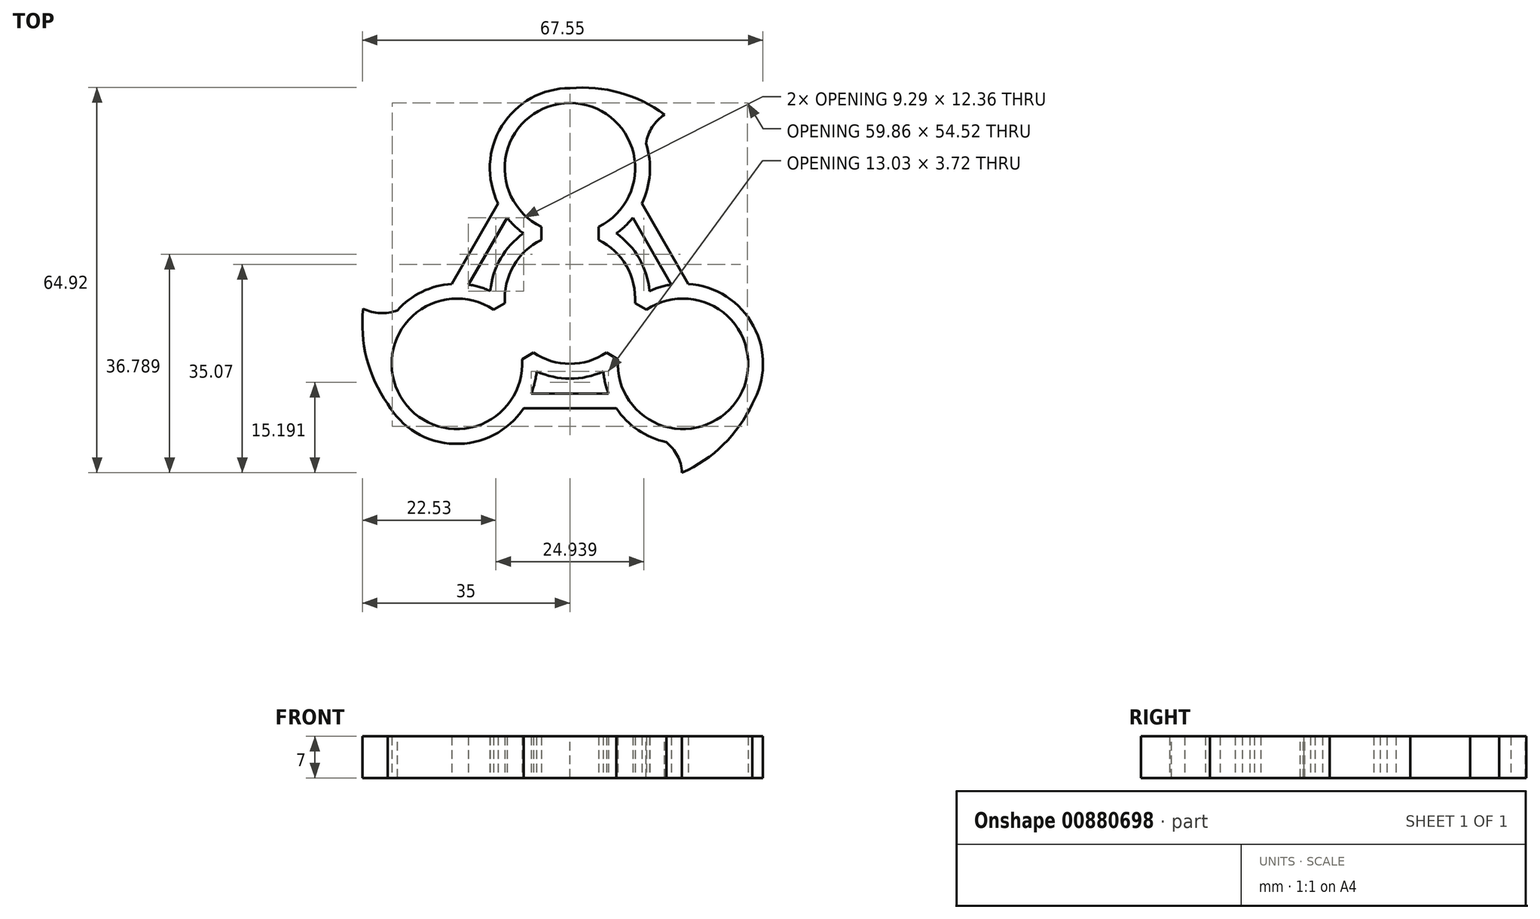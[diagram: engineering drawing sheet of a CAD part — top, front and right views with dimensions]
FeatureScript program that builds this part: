
annotation { "Feature Type Name" : "Feature", "Feature Type Description" : "" }
export const myFeature = defineFeature(function(context is Context, id is Id, definition is map)
    precondition{}
    {
        {
            var Q0;
            Q0=qCreatedBy(makeId("Top.planeOp"),FACE);
            var sketch = newSketch(context, id + "F0", { "sketchPlane" : qUnion([Q0])});
            skArc(sketch, "E0", {"start": v(-6.15, -9.12) * mm, "mid": v(0, -11) * mm, "end": v(6.15, -9.12) * mm});
            skLineSegment(sketch, "E1", {"start": v(0, 0) * mm, "end": v(0, 22) * mm});
            skArc(sketch, "E2", {"start": v(4.83, 12.12) * mm, "mid": v(0, 33) * mm, "end": v(-4.83, 12.12) * mm});
            skArc(sketch, "E3.1.0", {"start": v(-12.9, -1.88) * mm, "mid": v(-28.58, -16.5) * mm, "end": v(-8.08, -10.24) * mm});
            skArc(sketch, "E3.2.0", {"start": v(8.08, -10.24) * mm, "mid": v(28.58, -16.5) * mm, "end": v(12.9, -1.88) * mm});
            skArc(sketch, "E4", {"start": v(-5.61, -12.28) * mm, "mid": v(0, -13.5) * mm, "end": v(5.61, -12.28) * mm});
            skArc(sketch, "E5", {"start": v(7.83, 11) * mm, "mid": v(0, 35.5) * mm, "end": v(-7.83, 11) * mm});
            skArc(sketch, "E6.1.0", {"start": v(-13.44, 1.28) * mm, "mid": v(-32.04, -14.69) * mm, "end": v(-7.83, -18.5) * mm});
            skArc(sketch, "E6.2.0", {"start": v(5.61, -12.28) * mm, "mid": v(5.93, -14.17) * mm, "end": v(6.51, -16) * mm});
            skArc(sketch, "E7.trimOffspring", {"start": v(13.44, 1.28) * mm, "mid": v(11.7, 6.75) * mm, "end": v(7.83, 11) * mm});
            skArc(sketch, "E8.trimOffspring", {"start": v(-7.83, 11) * mm, "mid": v(-11.7, 6.75) * mm, "end": v(-13.44, 1.28) * mm});
            skLineSegment(sketch, "E9", {"start": v(-7.83, 11) * mm, "end": v(-4.83, 11) * mm});
            skLineSegment(sketch, "E10", {"start": v(-4.83, 11) * mm, "end": v(-4.83, 9.88) * mm});
            skLineSegment(sketch, "E11", {"start": v(-4.83, 9.88) * mm, "end": v(-4.83, 12.12) * mm});
            skLineSegment(sketch, "E12.1.0", {"start": v(-6.15, -9.12) * mm, "end": v(-8.08, -10.24) * mm});
            skLineSegment(sketch, "E12.2.0", {"start": v(10.97, -0.76) * mm, "end": v(12.9, -1.88) * mm});
            skLineSegment(sketch, "E13", {"start": v(7.83, 11) * mm, "end": v(4.83, 11) * mm});
            skLineSegment(sketch, "E14", {"start": v(4.83, 11) * mm, "end": v(4.83, 9.88) * mm});
            skLineSegment(sketch, "E15", {"start": v(4.83, 9.88) * mm, "end": v(4.83, 12.12) * mm});
            skLineSegment(sketch, "E16.1.0", {"start": v(-10.97, -0.76) * mm, "end": v(-12.9, -1.88) * mm});
            skLineSegment(sketch, "E16.2.0", {"start": v(6.15, -9.12) * mm, "end": v(8.08, -10.24) * mm});
            skLineSegment(sketch, "E17", {"start": v(0, 0) * mm, "end": v(0, -16) * mm});
            skLineSegment(sketch, "E18", {"start": v(0, -16) * mm, "end": v(6.51, -16) * mm});
            skLineSegment(sketch, "E19", {"start": v(6.51, -16) * mm, "end": v(-6.51, -16) * mm});
            skLineSegment(sketch, "E20.trimOffspring", {"start": v(7.83, -18.5) * mm, "end": v(-7.83, -18.5) * mm});
            skArc(sketch, "E21.trimOffspring", {"start": v(7.83, -18.5) * mm, "mid": v(32.04, -14.69) * mm, "end": v(13.44, 1.28) * mm});
            skArc(sketch, "E22.trimOffspring", {"start": v(-6.51, -16) * mm, "mid": v(-5.93, -14.17) * mm, "end": v(-5.61, -12.28) * mm});
            skArc(sketch, "E23.trimOffspring", {"start": v(10.97, -0.76) * mm, "mid": v(9.53, 5.5) * mm, "end": v(4.83, 9.88) * mm});
            skArc(sketch, "E24.trimOffspring", {"start": v(-4.83, 9.88) * mm, "mid": v(-9.53, 5.5) * mm, "end": v(-10.97, -0.76) * mm});
            skLineSegment(sketch, "E25.1.0", {"start": v(13.86, 8) * mm, "end": v(10.6, 13.64) * mm});
            skLineSegment(sketch, "E25.1.1", {"start": v(10.6, 13.64) * mm, "end": v(17.11, 2.36) * mm});
            skLineSegment(sketch, "E25.1.2", {"start": v(12.1, 16.03) * mm, "end": v(19.94, 2.47) * mm});
            skLineSegment(sketch, "E25.2.0", {"start": v(-13.86, 8) * mm, "end": v(-17.11, 2.36) * mm});
            skLineSegment(sketch, "E25.2.1", {"start": v(-17.11, 2.36) * mm, "end": v(-10.6, 13.64) * mm});
            skLineSegment(sketch, "E25.2.2", {"start": v(-19.94, 2.47) * mm, "end": v(-12.1, 16.03) * mm});
            skSolve(sketch);
        }
        {
            var Q0;
            {var subQ6=sQuery(id+"F0.wireOp",EDGE,"E25.2.2");Q0=makeQuery(id+"F0.imprint","IMPRINT",FACE,{"disambiguationData":[TD([[makeQuery(id+"F0.imprint","IMPRINT",EDGE,{"derivedFrom":subQ6}),-1.0]])]});}
            var Q1;
            {var subQ4=sQuery(id+"F0.wireOp",EDGE,"E2");Q1=makeQuery(id+"F0.imprint","IMPRINT",FACE,{"disambiguationData":[TD([[makeQuery(id+"F0.imprint","IMPRINT",EDGE,{"derivedFrom":subQ4}),-1.0]])]});}
            var Q2;
            {var subQ6=sQuery(id+"F0.wireOp",EDGE,"E25.1.2");Q2=makeQuery(id+"F0.imprint","IMPRINT",FACE,{"disambiguationData":[TD([[makeQuery(id+"F0.imprint","IMPRINT",EDGE,{"derivedFrom":subQ6}),-1.0]])]});}
            var Q3;
            Q3=makeQuery(id+"F0.imprint","IMPRINT",FACE,{"disambiguationData":[TD([[makeQuery(id+"F0.imprint","IMPRINT",EDGE,{"derivedFrom":sQuery(id+"F0.wireOp",EDGE,"E3.1.0")}),-1.0]])]});
            extrude(context, id + "F1", {"entities" : qUnion([Q0, Q1, Q2, Q3]), "depth" : 7 * mm, "offsetDistance" : 25 * mm});
        }
        {
            var Q0;
            Q0=makeQuery(id+"F1.opExtrude","CAP_FACE",FACE,{"disambiguationData":[OSD([sQuery(id+"F0.wireOp",EDGE,"E0"),sQuery(id+"F0.wireOp",EDGE,"E2"),sQuery(id+"F0.wireOp",EDGE,"E3.1.0"),sQuery(id+"F0.wireOp",EDGE,"E3.2.0"),sQuery(id+"F0.wireOp",EDGE,"E4"),sQuery(id+"F0.wireOp",EDGE,"E5"),sQuery(id+"F0.wireOp",EDGE,"E6.1.0"),sQuery(id+"F0.wireOp",EDGE,"E6.2.0"),sQuery(id+"F0.wireOp",EDGE,"E7.trimOffspring"),sQuery(id+"F0.wireOp",EDGE,"E8.trimOffspring"),sQuery(id+"F0.wireOp",EDGE,"E11"),sQuery(id+"F0.wireOp",EDGE,"E12.1.0"),sQuery(id+"F0.wireOp",EDGE,"E12.2.0"),sQuery(id+"F0.wireOp",EDGE,"E15"),sQuery(id+"F0.wireOp",EDGE,"E16.1.0"),sQuery(id+"F0.wireOp",EDGE,"E16.2.0"),sQuery(id+"F0.wireOp",EDGE,"E19"),sQuery(id+"F0.wireOp",EDGE,"E20.trimOffspring"),sQuery(id+"F0.wireOp",EDGE,"E21.trimOffspring"),sQuery(id+"F0.wireOp",EDGE,"E22.trimOffspring"),sQuery(id+"F0.wireOp",EDGE,"E23.trimOffspring"),sQuery(id+"F0.wireOp",EDGE,"E24.trimOffspring"),sQuery(id+"F0.wireOp",EDGE,"E25.1.1"),sQuery(id+"F0.wireOp",EDGE,"E25.1.2"),sQuery(id+"F0.wireOp",EDGE,"E25.2.1"),sQuery(id+"F0.wireOp",EDGE,"E25.2.2")])],"isStart":false});
            var sketch = newSketch(context, id + "F2", { "sketchPlane" : qUnion([Q0])});
            skArc(sketch, "E26", {"start": v(15.95, 31.04) * mm, "mid": v(8.38, 34.72) * mm, "end": v(0, 35.5) * mm});
            skLineSegment(sketch, "E27", {"start": v(0, 22) * mm, "end": v(30.45, 22) * mm});
            skArc(sketch, "E28", {"start": v(15.95, 31.04) * mm, "mid": v(13.01, 26.98) * mm, "end": v(13.5, 22) * mm});
            skArc(sketch, "E29.1.0", {"start": v(-34.86, -1.7) * mm, "mid": v(-34.26, -10.1) * mm, "end": v(-30.74, -17.75) * mm});
            skArc(sketch, "E29.1.1", {"start": v(-34.86, -1.7) * mm, "mid": v(-29.88, -2.22) * mm, "end": v(-25.8, 0.7) * mm});
            skArc(sketch, "E29.2.0", {"start": v(18.9, -29.33) * mm, "mid": v(25.88, -24.62) * mm, "end": v(30.74, -17.75) * mm});
            skArc(sketch, "E29.2.1", {"start": v(18.9, -29.33) * mm, "mid": v(16.86, -24.76) * mm, "end": v(12.3, -22.7) * mm});
            skPoint(sketch, "E29.center", {"position": v(0, 0) * mm});
            skSolve(sketch);
        }
        {
            var Q0;
            {var subQ0=sQuery(id+"F2.wireOp",EDGE,"E26");Q0=makeQuery(id+"F2.imprint","IMPRINT",FACE,{"disambiguationData":[TD([[makeQuery(id+"F2.imprint","IMPRINT",EDGE,{"derivedFrom":subQ0}),1.0]])]});}
            var Q1;
            {var subQ0=sQuery(id+"F2.wireOp",EDGE,"E29.1.0");Q1=makeQuery(id+"F2.imprint","IMPRINT",FACE,{"disambiguationData":[TD([[makeQuery(id+"F2.imprint","IMPRINT",EDGE,{"derivedFrom":subQ0}),1.0]])]});}
            var Q2;
            {var subQ0=sQuery(id+"F2.wireOp",EDGE,"E29.2.0");Q2=makeQuery(id+"F2.imprint","IMPRINT",FACE,{"disambiguationData":[TD([[makeQuery(id+"F2.imprint","IMPRINT",EDGE,{"derivedFrom":subQ0}),1.0]])]});}
            extrude(context, id + "F3", {"entities" : qUnion([Q0, Q1, Q2]), "operationType" : NewBodyOperationType.ADD, "oppositeDirection" : true, "depth" : 7 * mm, "offsetDistance" : 25 * mm});
        }
    });
